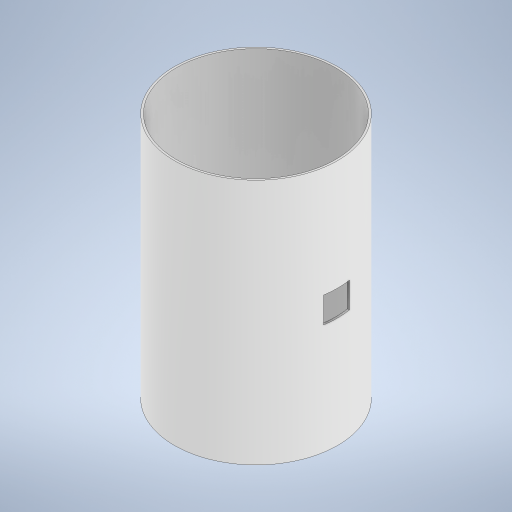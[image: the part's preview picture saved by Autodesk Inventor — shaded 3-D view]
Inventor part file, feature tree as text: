
AUTODESK INVENTOR PART (.ipt)
format: ipt  version: 2024 (Build 280153000, 153)  size: 239,616 bytes
history: native  units: in
note: dims shown in document units (in); Inventor stores cm internally (conversion verified against a paired STEP export)
features: extrude x2, sketch x2
ambient origin geometry x8: Origin, YZ Plane, XZ Plane, XY Plane, X Axis, Y Axis, Z Axis, Center Point
bodies: Solid2 (feature_tree), Solid1 (feature_tree)
feature tree (4):
  extrude  "Extrusion1"  Depth=1.6142in
  extrude  "Extrusion2"  Depth=0.8268in
  sketch  "Sketch1"  dims[d0=1.5748in d1=1.6142in]
  sketch  "Sketch2"  dims[d2=0.8268in d3=0.0in d4=1.5748in d5=1.6142in d6=0.8268in d7=0.0in]
